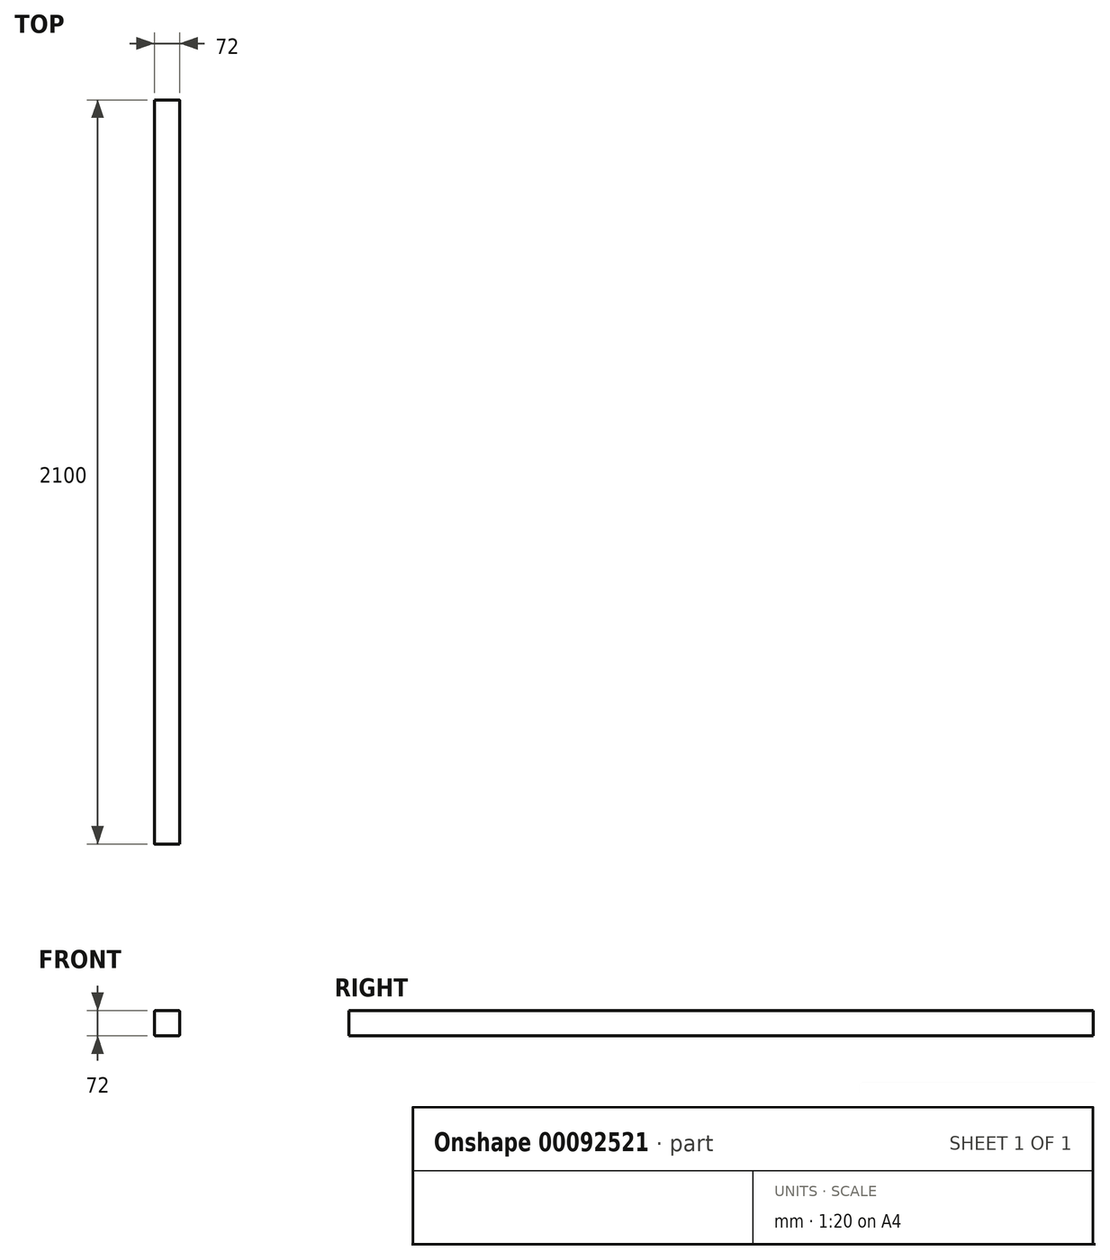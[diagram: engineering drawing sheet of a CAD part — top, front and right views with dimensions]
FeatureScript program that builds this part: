
annotation { "Feature Type Name" : "Feature", "Feature Type Description" : "" }
export const myFeature = defineFeature(function(context is Context, id is Id, definition is map)
    precondition{}
    {
        {
            var Q0;
            Q0=qCreatedBy(makeId("Front.planeOp"),FACE);
            var sketch = newSketch(context, id + "F0", { "sketchPlane" : qUnion([Q0])});
            skLineSegment(sketch, "E0.bottom", {"start": v(32, 36) * mm, "end": v(-32, 36) * mm});
            skLineSegment(sketch, "E0.top", {"start": v(32, -36) * mm, "end": v(-32, -36) * mm});
            skLineSegment(sketch, "E0.left", {"start": v(36, 32) * mm, "end": v(36, -32) * mm});
            skLineSegment(sketch, "E0.right", {"start": v(-36, 32) * mm, "end": v(-36, -32) * mm});
            skPoint(sketch, "E0.middle", {"position": v(0, 0) * mm});
            skPoint(sketch, "E1.visualSharp", {"position": v(-36, 36) * mm});
            skArc(sketch, "E1.filletArc", {"start": v(-32, 36) * mm, "mid": v(-34.83, 34.83) * mm, "end": v(-36, 32) * mm});
            skPoint(sketch, "E2.visualSharp", {"position": v(36, 36) * mm});
            skArc(sketch, "E2.filletArc", {"start": v(36, 32) * mm, "mid": v(34.83, 34.83) * mm, "end": v(32, 36) * mm});
            skPoint(sketch, "E3.visualSharp", {"position": v(36, -36) * mm});
            skArc(sketch, "E3.filletArc", {"start": v(32, -36) * mm, "mid": v(34.83, -34.83) * mm, "end": v(36, -32) * mm});
            skPoint(sketch, "E4.visualSharp", {"position": v(-36, -36) * mm});
            skArc(sketch, "E4.filletArc", {"start": v(-36, -32) * mm, "mid": v(-34.83, -34.83) * mm, "end": v(-32, -36) * mm});
            skSolve(sketch);
        }
        {
            var Q0;
            Q0 = qSketchRegion(id + "F0", true);
            extrude(context, id + "F1", {"entities" : qUnion([Q0]), "depth" : 2100 * mm});
        }
        {
            var Q0;
            Q0=makeQuery(id+"F1.opExtrude","SWEPT_FACE",FACE,{"disambiguationData":[OSD([sQuery(id+"F0.wireOp",EDGE,"E0.bottom")])]});
            var sketch = newSketch(context, id + "F2", { "sketchPlane" : qUnion([Q0])});
            skLineSegment(sketch, "E5", {"start": v(0, 0) * mm, "end": v(0, -2100) * mm, "construction": true});
            skLineSegment(sketch, "E6", {"start": v(-32, -300) * mm, "end": v(32, -300) * mm, "construction": true});
            skSolve(sketch);
        }
    });
